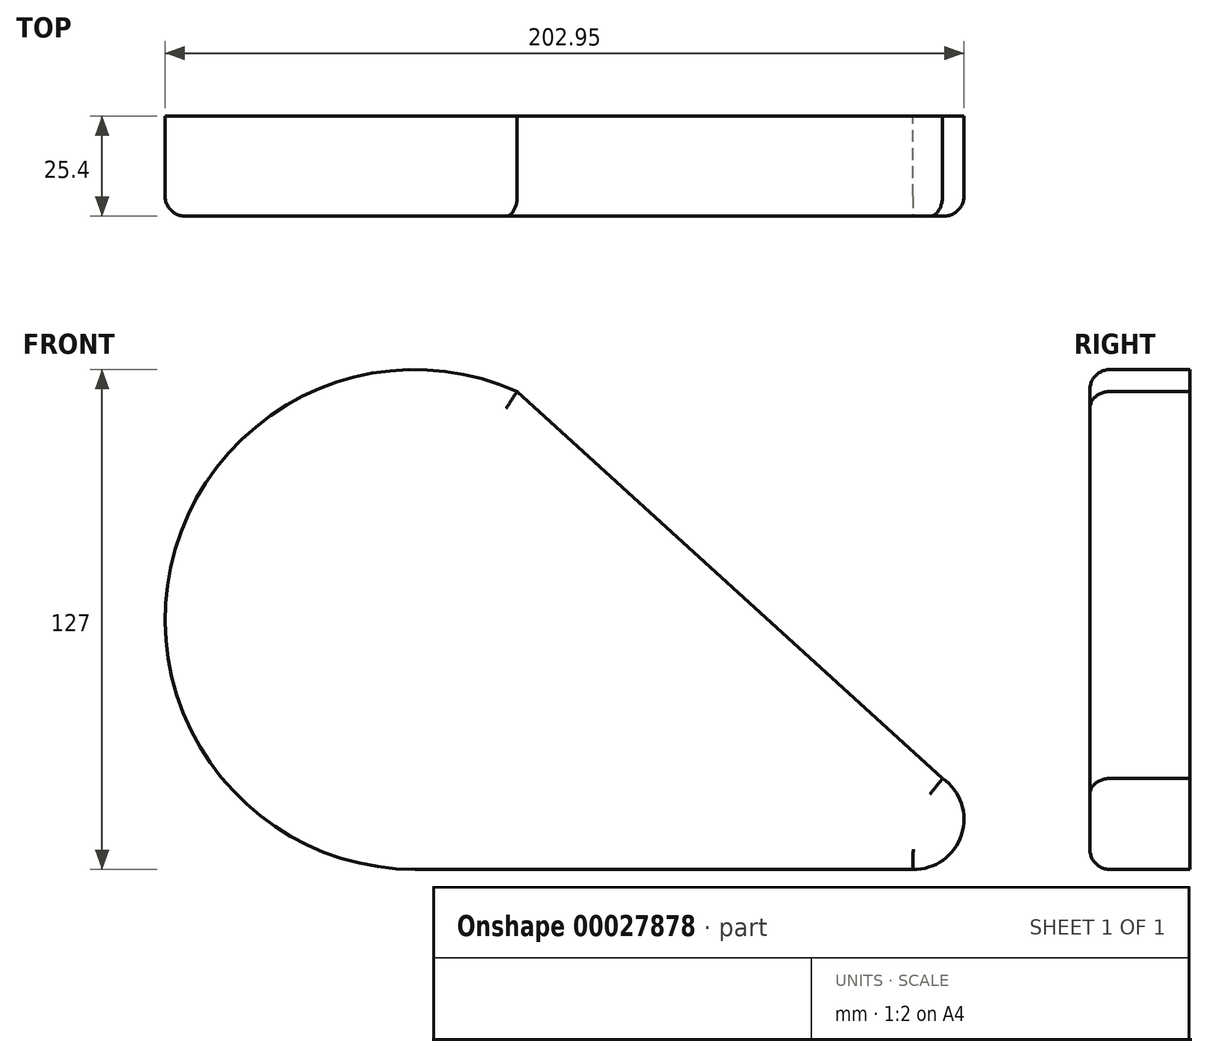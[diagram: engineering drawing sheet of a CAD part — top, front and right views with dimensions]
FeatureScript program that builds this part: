
annotation { "Feature Type Name" : "Feature", "Feature Type Description" : "" }
export const myFeature = defineFeature(function(context is Context, id is Id, definition is map)
    precondition{}
    {
        {
            var Q0;
            Q0=qCreatedBy(makeId("Front.planeOp"),FACE);
            var sketch = newSketch(context, id + "F0", { "sketchPlane" : qUnion([Q0])});
            skCircle(sketch, "E0", {"center": v(0, 0) * mm, "radius": 63.5 * mm});
            skLineSegment(sketch, "E1", {"start": v(0, -63.5) * mm, "end": v(127, -63.5) * mm});
            skCircle(sketch, "E2", {"center": v(126.75, -50.8) * mm, "radius": 12.7 * mm});
            skPoint(sketch, "E2.second.point", {"position": v(127, -38.1) * mm});
            skPoint(sketch, "E2.third.point", {"position": v(136.45, -42.6) * mm});
            skLineSegment(sketch, "E3", {"start": v(25.97, 57.95) * mm, "end": v(136.45, -42.6) * mm});
            skSolve(sketch);
        }
        {
            var Q0;
            {var subQ0=sQuery(id+"F0.wireOp",EDGE,"E2");var subQ1=sQuery(id+"F0.wireOp",EDGE,"E1");var subQ3=makeQuery(id+"F0.imprint","INTERSECT",VERTEX,{"disambiguationData":[OD(0.0)],"derivedFrom":[subQ1,subQ0]});Q0=makeQuery(id+"F0.imprint","IMPRINT",FACE,{"disambiguationData":[TD([[makeQuery(id+"F0.imprint","IMPRINT",EDGE,{"disambiguationData":[TD([[subQ3,1.0]])],"derivedFrom":subQ1}),-1.0]])]});}
            var Q1;
            {var subQ0=sQuery(id+"F0.wireOp",EDGE,"E3");var subQ1=sQuery(id+"F0.wireOp",EDGE,"E2");var subQ3=makeQuery(id+"F0.imprint","INTERSECT",VERTEX,{"disambiguationData":[OD(0.0)],"derivedFrom":[subQ1,subQ0]});Q1=makeQuery(id+"F0.imprint","IMPRINT",FACE,{"disambiguationData":[TD([[makeQuery(id+"F0.imprint","IMPRINT",EDGE,{"disambiguationData":[TD([[subQ3,-1.0]])],"derivedFrom":subQ1}),1.0]])]});}
            var Q2;
            {var subQ3=sQuery(id+"F0.wireOp",EDGE,"E0");var subQ5=sQuery(id+"F0.wireOp",EDGE,"E1");var subQ7=makeQuery(id+"F0.imprint","INTERSECT",VERTEX,{"derivedFrom":[subQ3,subQ5]});Q2=makeQuery(id+"F0.imprint","IMPRINT",FACE,{"disambiguationData":[TD([[makeQuery(id+"F0.imprint","IMPRINT",EDGE,{"disambiguationData":[TD([[subQ7,-1.0]])],"derivedFrom":subQ3}),-1.0]])]});}
            var Q3;
            {var subQ1=sQuery(id+"F0.wireOp",EDGE,"E2");var subQ4=sQuery(id+"F0.wireOp",EDGE,"E1");var subQ5=makeQuery(id+"F0.imprint","INTERSECT",VERTEX,{"disambiguationData":[OD(0.0)],"derivedFrom":[subQ4,subQ1]});Q3=makeQuery(id+"F0.imprint","IMPRINT",FACE,{"disambiguationData":[TD([[makeQuery(id+"F0.imprint","IMPRINT",EDGE,{"disambiguationData":[TD([[subQ5,1.0]])],"derivedFrom":subQ4}),1.0]])]});}
            var Q4;
            {var subQ1=sQuery(id+"F0.wireOp",EDGE,"E0");var subQ4=makeQuery(id+"F0.imprint","INTERSECT",VERTEX,{"derivedFrom":[subQ1,sQuery(id+"F0.wireOp",EDGE,"E1")]});Q4=makeQuery(id+"F0.imprint","IMPRINT",FACE,{"disambiguationData":[TD([[makeQuery(id+"F0.imprint","IMPRINT",EDGE,{"disambiguationData":[TD([[subQ4,1.0]])],"derivedFrom":subQ1}),1.0]])]});}
            extrude(context, id + "F1", {"entities" : qUnion([Q0, Q1, Q2, Q3, Q4]), "depth" : 25.4 * mm});
        }
        {
            var Q0;
            Q0=makeQuery(id+"F1.opExtrude","CAP_FACE",FACE,{"disambiguationData":[OSD([sQuery(id+"F0.wireOp",EDGE,"E0"),sQuery(id+"F0.wireOp",EDGE,"E1"),sQuery(id+"F0.wireOp",EDGE,"E2"),sQuery(id+"F0.wireOp",EDGE,"E3")])],"isStart":false});
            fillet(context, id + "F2", {"entities" : qUnion([Q0]), "radius" : 5.08 * mm, "tangentPropagation" : true, "allowEdgeOverflow" : false});
        }
    });
